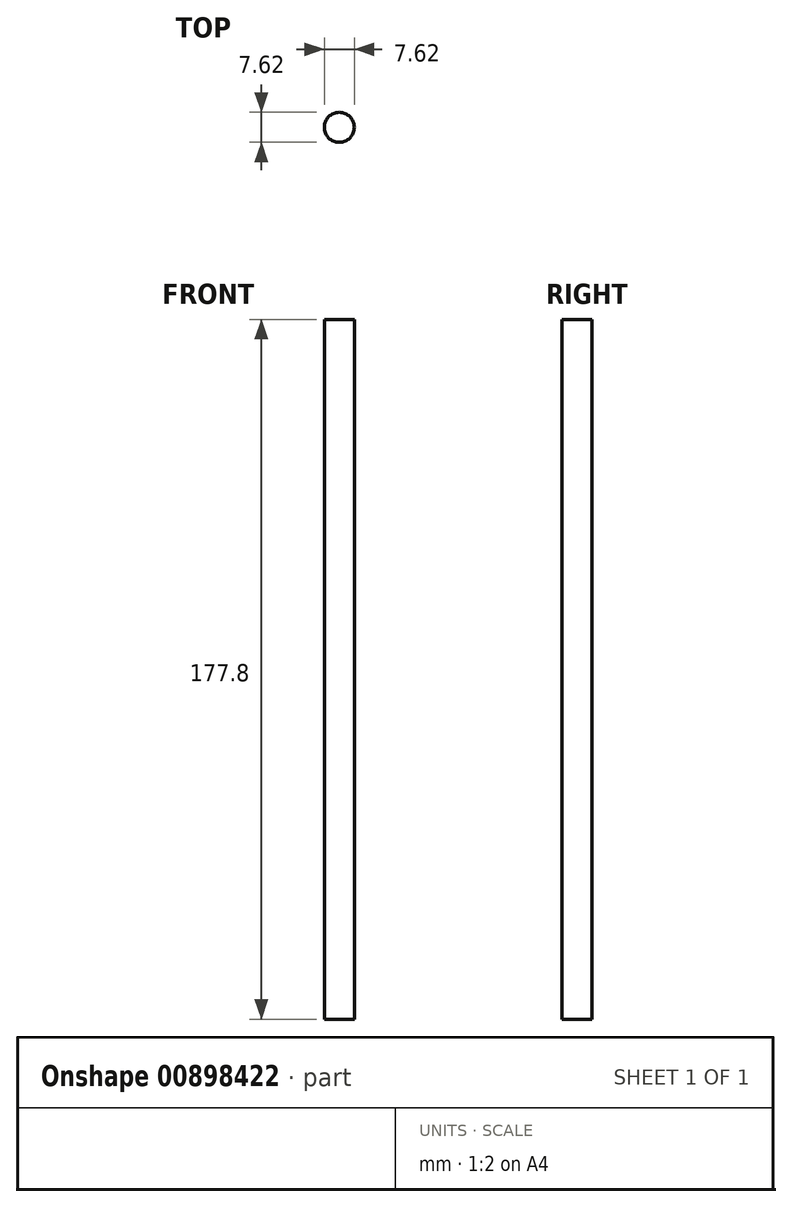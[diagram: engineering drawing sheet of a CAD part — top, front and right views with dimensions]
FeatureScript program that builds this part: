
annotation { "Feature Type Name" : "Feature", "Feature Type Description" : "" }
export const myFeature = defineFeature(function(context is Context, id is Id, definition is map)
    precondition{}
    {
        {
            var Q0;
            Q0=qCreatedBy(makeId("Top.planeOp"),FACE);
            var sketch = newSketch(context, id + "F0", { "sketchPlane" : qUnion([Q0])});
            skCircle(sketch, "E0", {"center": v(-68.28, -35.74) * mm, "radius": 3.81 * mm});
            skSolve(sketch);
        }
        {
            var Q0;
            Q0 = qConstructionFilter(qBodyType(qCreatedBy(id + "F0" ,EDGE), BodyType.WIRE), ConstructionObject.NO);
            extrude(context, id + "F1", {"bodyType" : ToolBodyType.SURFACE, "surfaceEntities" : qUnion([Q0]), "depth" : 177.8 * mm, "offsetDistance" : 25.4 * mm});
        }
    });
